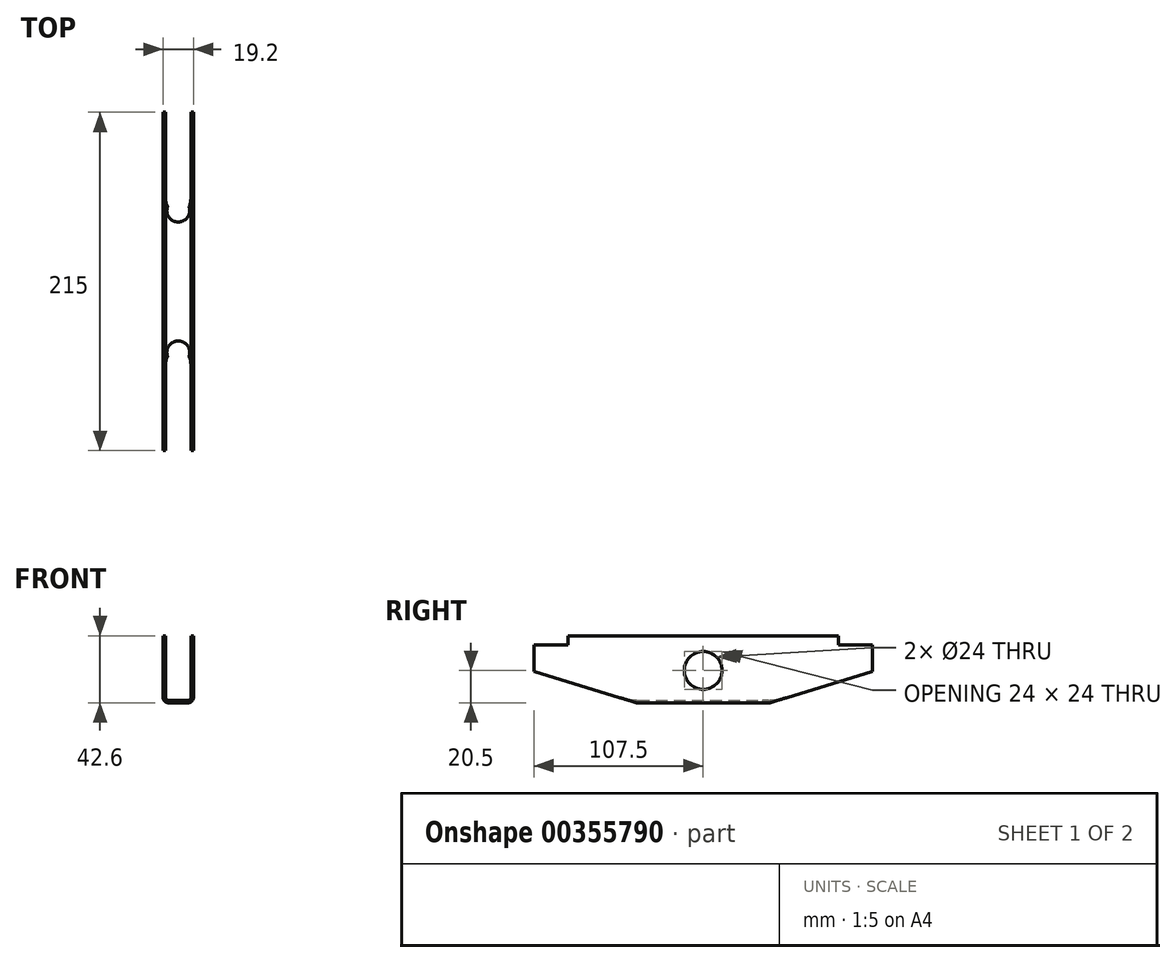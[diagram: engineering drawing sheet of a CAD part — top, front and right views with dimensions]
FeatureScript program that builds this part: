
annotation { "Feature Type Name" : "Feature", "Feature Type Description" : "" }
export const myFeature = defineFeature(function(context is Context, id is Id, definition is map)
    precondition{}
    {
        {
            var Q0;
            Q0=qCreatedBy(makeId("Front.planeOp"),FACE);
            var sketch = newSketch(context, id + "F0", { "sketchPlane" : qUnion([Q0])});
            skLineSegment(sketch, "E0", {"start": v(0, 0) * mm, "end": v(-6.4, 0) * mm});
            skLineSegment(sketch, "E1", {"start": v(-9.6, 3.2) * mm, "end": v(-9.6, 42.6) * mm});
            skLineSegment(sketch, "E2", {"start": v(-9.6, 42.6) * mm, "end": v(-8, 42.6) * mm});
            skLineSegment(sketch, "E3", {"start": v(-8, 42.6) * mm, "end": v(-8, 3.2) * mm});
            skLineSegment(sketch, "E4", {"start": v(-6.4, 1.6) * mm, "end": v(0, 1.6) * mm});
            skPoint(sketch, "E5.visualSharp", {"position": v(-8, 1.6) * mm});
            skArc(sketch, "E5.filletArc", {"start": v(-8, 3.2) * mm, "mid": v(-7.53, 2.07) * mm, "end": v(-6.4, 1.6) * mm});
            skPoint(sketch, "E6.visualSharp", {"position": v(-9.6, 0) * mm});
            skArc(sketch, "E6.filletArc", {"start": v(-9.6, 3.2) * mm, "mid": v(-8.66, 0.94) * mm, "end": v(-6.4, 0) * mm});
            skLineSegment(sketch, "E7", {"start": v(0, 0) * mm, "end": v(0, 33.76) * mm, "construction": true});
            skLineSegment(sketch, "E8.MirrorCS", {"start": v(9.6, 42.6) * mm, "end": v(8, 42.6) * mm});
            skArc(sketch, "E9.MirrorCS", {"start": v(8, 3.2) * mm, "mid": v(7.53, 2.07) * mm, "end": v(6.4, 1.6) * mm});
            skArc(sketch, "E10.MirrorCS", {"start": v(9.6, 3.2) * mm, "mid": v(8.66, 0.94) * mm, "end": v(6.4, 0) * mm});
            skLineSegment(sketch, "E11.MirrorCS", {"start": v(0, 0) * mm, "end": v(6.4, 0) * mm});
            skLineSegment(sketch, "E12.MirrorCS", {"start": v(9.6, 3.2) * mm, "end": v(9.6, 42.6) * mm});
            skPoint(sketch, "E13.MirrorP", {"position": v(8, 1.6) * mm});
            skPoint(sketch, "E14.MirrorP", {"position": v(9.6, 0) * mm});
            skLineSegment(sketch, "E15.MirrorCS", {"start": v(8, 42.6) * mm, "end": v(8, 3.2) * mm});
            skLineSegment(sketch, "E16.MirrorCS", {"start": v(6.4, 1.6) * mm, "end": v(0, 1.6) * mm});
            skSolve(sketch);
        }
        {
            var Q0;
            Q0=qSketchRegion(id+"F0",true);
            extrude(context, id + "F1", {"entities" : qUnion([Q0]), "endBound" : BoundingType.SYMMETRIC, "depth" : 215 * mm});
        }
        {
            var Q0;
            Q0=makeQuery(id+"F1.opExtrude","SWEPT_FACE",FACE,{"disambiguationData":[OSD([sQuery(id+"F0.wireOp",EDGE,"E1")])]});
            var sketch = newSketch(context, id + "F2", { "sketchPlane" : qUnion([Q0])});
            skLineSegment(sketch, "E17.bottom", {"start": v(-107.5, 42.6) * mm, "end": v(-86, 42.6) * mm});
            skLineSegment(sketch, "E17.top", {"start": v(-107.5, 36.6) * mm, "end": v(-86, 36.6) * mm});
            skLineSegment(sketch, "E17.left", {"start": v(-107.5, 42.6) * mm, "end": v(-107.5, 36.6) * mm});
            skLineSegment(sketch, "E17.right", {"start": v(-86, 42.6) * mm, "end": v(-86, 36.6) * mm});
            skLineSegment(sketch, "E18", {"start": v(-107.5, 20) * mm, "end": v(-42.5, 0) * mm});
            skLineSegment(sketch, "E19", {"start": v(-42.5, 0) * mm, "end": v(-107.5, 0) * mm});
            skLineSegment(sketch, "E20", {"start": v(-107.5, 0) * mm, "end": v(-107.5, 20) * mm});
            skLineSegment(sketch, "E21", {"start": v(0, 0) * mm, "end": v(0, 57.1) * mm, "construction": true});
            skLineSegment(sketch, "E22.MirrorCS", {"start": v(107.5, 0) * mm, "end": v(107.5, 20) * mm});
            skLineSegment(sketch, "E23.MirrorCS", {"start": v(42.5, 0) * mm, "end": v(107.5, 0) * mm});
            skLineSegment(sketch, "E24.MirrorCS", {"start": v(107.5, 20) * mm, "end": v(42.5, 0) * mm});
            skLineSegment(sketch, "E25.MirrorCS", {"start": v(86, 42.6) * mm, "end": v(86, 36.6) * mm});
            skLineSegment(sketch, "E26.MirrorCS", {"start": v(107.5, 42.6) * mm, "end": v(107.5, 36.6) * mm});
            skLineSegment(sketch, "E27.MirrorCS", {"start": v(107.5, 42.6) * mm, "end": v(86, 42.6) * mm});
            skLineSegment(sketch, "E28.MirrorCS", {"start": v(107.5, 36.6) * mm, "end": v(86, 36.6) * mm});
            skCircle(sketch, "E29", {"center": v(0, 20.5) * mm, "radius": 12 * mm});
            skSolve(sketch);
        }
        {
            var Q0;
            Q0=qSketchRegion(id+"F2",true);
            extrude(context, id + "F3", {"entities" : qUnion([Q0]), "operationType" : NewBodyOperationType.REMOVE, "oppositeDirection" : true, "depth" : 25 * mm});
        }
        {
            var Q0;
            Q0=makeQuery(id+"F1.opExtrude","SWEPT_FACE",FACE,{"disambiguationData":[OSD([sQuery(id+"F0.wireOp",EDGE,"E0"),sQuery(id+"F0.wireOp",EDGE,"E11.MirrorCS")])]});
            var sketch = newSketch(context, id + "F4", { "sketchPlane" : qUnion([Q0])});
            skLineSegment(sketch, "E30", {"start": v(0, 0) * mm, "end": v(0, -71.9) * mm, "construction": true});
            skCircle(sketch, "E31", {"center": v(0, -45) * mm, "radius": 7.25 * mm});
            skLineSegment(sketch, "E32", {"start": v(0, 0) * mm, "end": v(-19.35, 0) * mm, "construction": true});
            skCircle(sketch, "E33.MirrorC", {"center": v(0, 45) * mm, "radius": 7.25 * mm});
            skSolve(sketch);
        }
        {
            var Q0;
            Q0=qSketchRegion(id+"F4",true);
            extrude(context, id + "F5", {"entities" : qUnion([Q0]), "operationType" : NewBodyOperationType.REMOVE, "oppositeDirection" : true, "depth" : 5 * mm});
        }
    });
